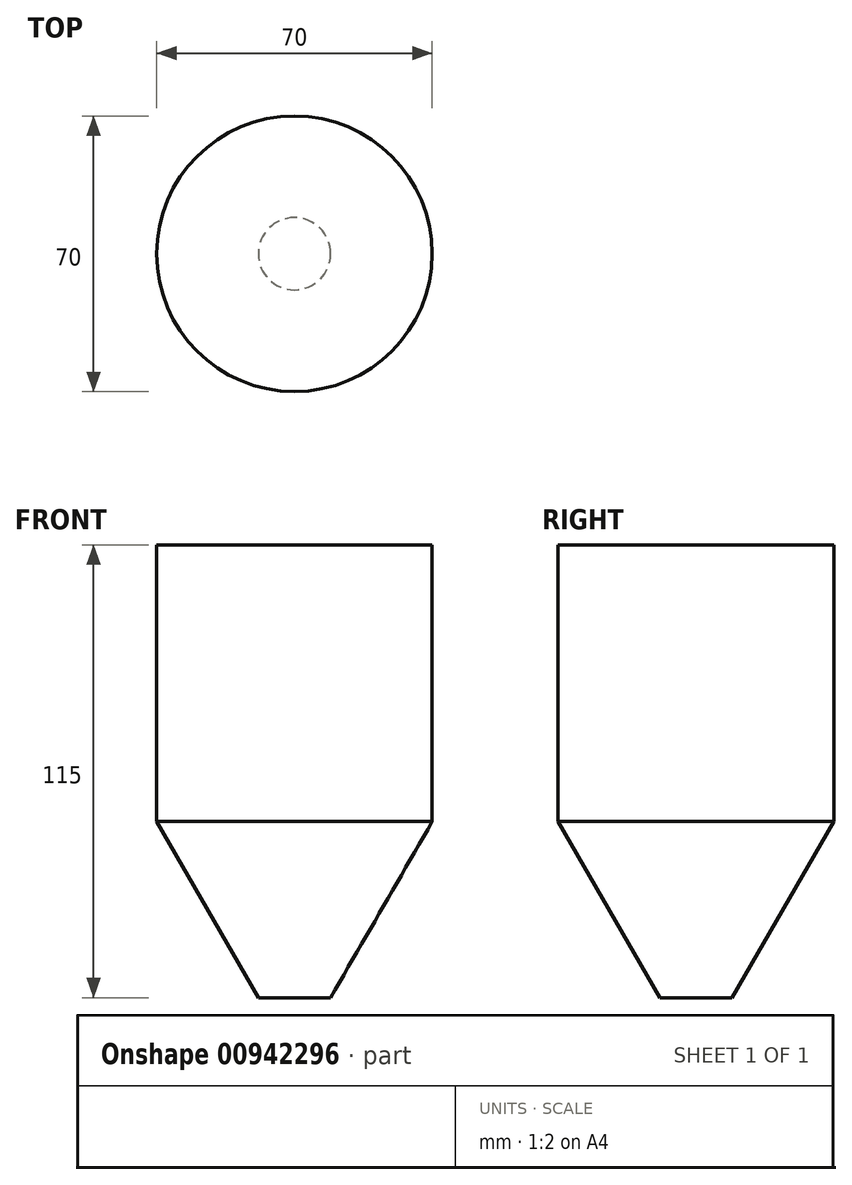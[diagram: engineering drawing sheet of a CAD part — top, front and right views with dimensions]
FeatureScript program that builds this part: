
annotation { "Feature Type Name" : "Feature", "Feature Type Description" : "" }
export const myFeature = defineFeature(function(context is Context, id is Id, definition is map)
    precondition{}
    {
        {
            var Q0;
            Q0=qCreatedBy(makeId("Front.planeOp"),FACE);
            var sketch = newSketch(context, id + "F0", { "sketchPlane" : qUnion([Q0])});
            skLineSegment(sketch, "E0", {"start": v(0, 0) * mm, "end": v(9.18, 0) * mm});
            skLineSegment(sketch, "E1", {"start": v(9.18, 0) * mm, "end": v(35, 44.72) * mm});
            skLineSegment(sketch, "E2", {"start": v(35, 44.72) * mm, "end": v(35, 115) * mm});
            skLineSegment(sketch, "E3", {"start": v(35, 115) * mm, "end": v(0, 115) * mm});
            skLineSegment(sketch, "E4", {"start": v(0, 115) * mm, "end": v(0, 0) * mm});
            skSolve(sketch);
        }
        {
            var Q0;
            Q0 = qSketchRegion(id + "F0", true);
            var Q1;
            Q1=sQuery(id+"F0.wireOp",EDGE,"E4");
            revolve(context, id + "F1", {"surfaceOperationType" : NewSurfaceOperationType.NEW, "entities" : qUnion([Q0]), "axis" : qUnion([Q1]), "revolveType" : RevolveType.FULL});
        }
    });
